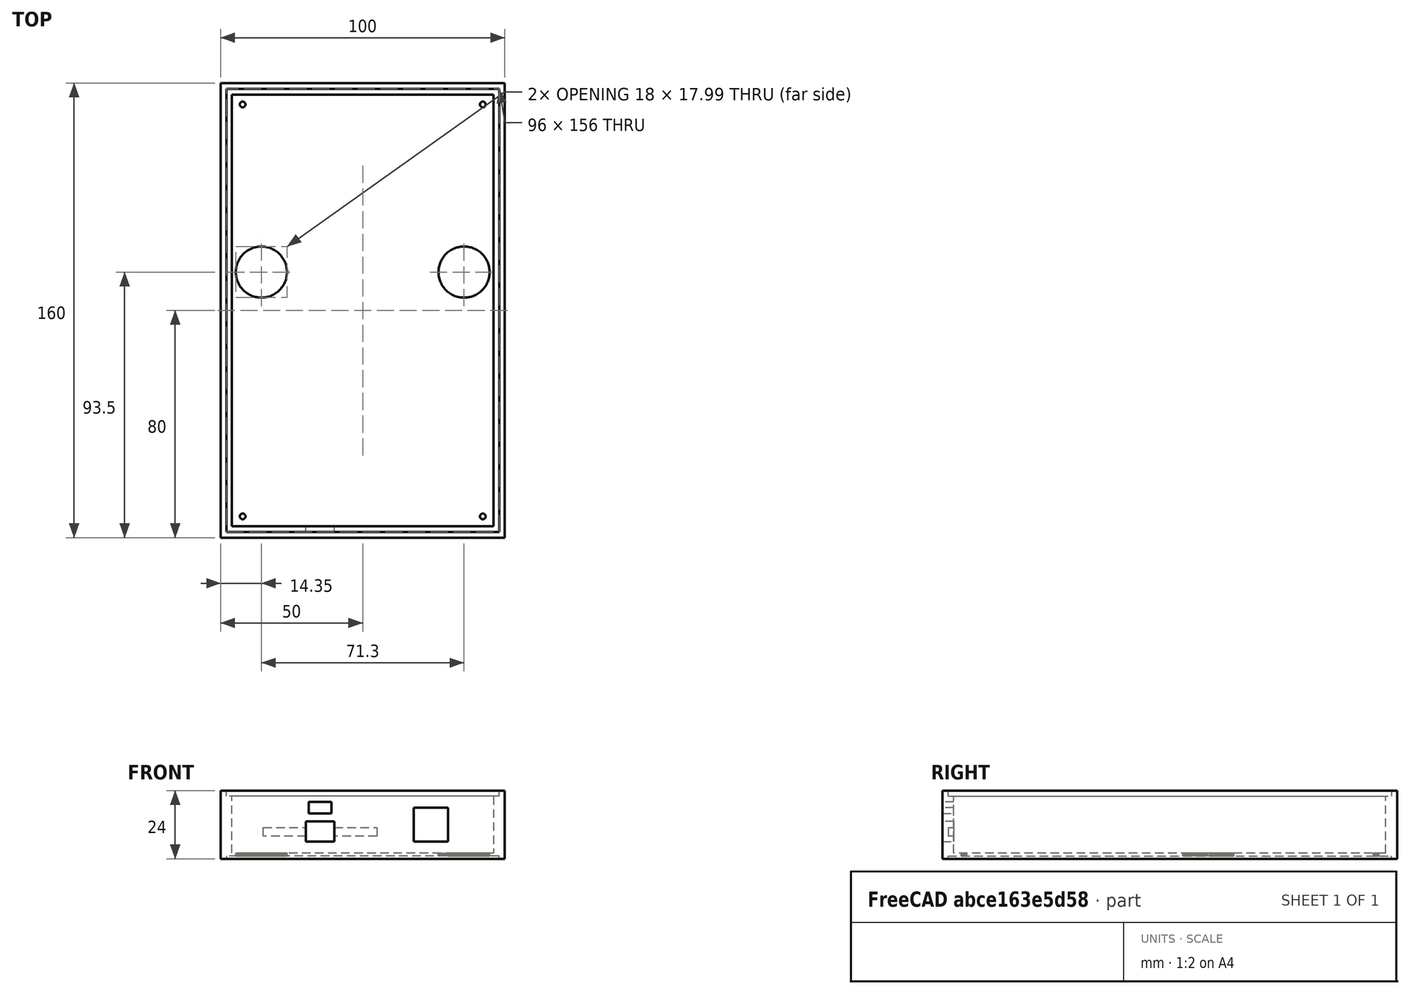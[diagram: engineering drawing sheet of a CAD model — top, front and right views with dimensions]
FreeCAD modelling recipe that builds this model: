
FCSTD DOCUMENT  (FreeCAD 0.19R24291 (Git))
Label: trueimage_10button_top_fixed
License: All rights reserved
LicenseURL: http://en.wikipedia.org/wiki/All_rights_reserved
objects: Part::Feature×1, Mesh::Feature×1, Part::Refine×1, Sketcher::SketchObject×1, PartDesign::Body×1, Part::Extrusion×1, Part::Cut×1
note: 6 computed .brp shape members not serialized (recipe doc carries the construction recipe); baked Part::Feature solids carry a one-line shape summary decoded from their .brp

FEATURE [Part::Feature] trueimage_10button_top_Body001
  shape: bbox 100 x 160 x 24 mm, 3168 faces, 0 solids (baked)
FEATURE [Mesh::Feature] trueimage_10button_top_Body  label="trueimage_10button_top-Body"
FEATURE [Part::Refine] trueimage_10button_top_Body001001
  Source = -> trueimage_10button_top_Body001
FEATURE [Sketcher::SketchObject] Sketch
  AttachmentOffset = pos=(0,0,73) rot=(0,0,1;0rad)
  FullyConstrained = true
  MapMode = 5
  Placement = pos=(0,-73,1.62e-14) rot=(1,0,0;1.5708rad)
  Support = -> [XZ_Plane]
  sketch-geometry (4):
    g0: LineSegment StartX=-35 StartY=11 StartZ=0 EndX=5 EndY=11 EndZ=0
    g1: LineSegment StartX=5 StartY=11 StartZ=0 EndX=5 EndY=8 EndZ=0
    g2: LineSegment StartX=5 StartY=8 StartZ=0 EndX=-35 EndY=8 EndZ=0
    g3: LineSegment StartX=-35 StartY=8 StartZ=0 EndX=-35 EndY=11 EndZ=0
  constraints (12):
    c: Coincident(g0,g1)
    c: Coincident(g1,g2)
    c: Coincident(g2,g3)
    c: Coincident(g3,g0)
    c: Horizontal(g0)
    c: Horizontal(g2)
    c: Vertical(g1)
    c: Vertical(g3)
    c: DistanceY(g1,g1) = 3
    c: DistanceX(g0,g0) = 40
    c: DistanceY(g-1,g1) = 8
    c: DistanceX(g0,g-1) = -5
FEATURE [PartDesign::Body] Body
  Group = -> [Sketch]
  Origin = -> Origin
FEATURE [Part::Extrusion] Extrude001
  Base = -> Sketch
  Dir = (0,-1,2e-16)
  DirMode = 2
  FaceMakerClass = Part::FaceMakerBullseye
  LengthFwd = 5
  LengthRev = -2
  Solid = true
  Symmetric = false
FEATURE [Part::Cut] Cut
  Base = -> trueimage_10button_top_Body001001
  Refine = true
  Tool = -> Extrude001
